# Revit family: QF_ELECTROLUXPROFESSIONAL_587184_PBOT30SDJO
name_source: partatom
category: Attrezzature speciali
units: mm (PartAtom-declared; Revit-internal decimal feet)

## family parameters
Basato su piano di lavoro = No
Condiviso = No
Punto di calcolo locali = No
Quota connettore circolare = Usa diametro
Sempre verticale = Sì
Taglio con vuoti quando caricato = No
Tipo di parte = Normale

## types (1)
- Standard
    Accessory = Sì
    Cold Water Size = 13 mm
    Compressed Air Pressure = 0.0 Pa
    Compressed Air Size = 0 mm
    Compressed Air Volume = 0.0 L/s
    Condensate Return Size = 25 mm
    Cycle = 50 Hz
    Depth Actual = 1000 mm  [stored 3.28084 ft]
    Descrizione = STEAM (ELEC) BOILING PAN,TILTING,300L,230V,FS,MARINE
    Direct Waste Size = 0 mm
    Gas Input Pressure = 0
    Gas KW = 0
    Gas Size = 0 mm
    HP = 0.3 HP
    Height Actual = 700 mm
    Hot Water Size = 13 mm
    Item Number = 587184
    Length Actual = 1500 mm  [stored 4.92126 ft]
    Modello = PBOT30SDJO
    Phase = 1
    Produttore = Electrolux Professional
    Prospetto di default = 0 mm  [stored 0 ft]
    Refrigerant Compressor Remote = Sì
    Refrigeration Liquid Line Size = 0 mm  [stored 0 ft]
    Refrigeration Suction Line Size = 0 mm  [stored 0 ft]
    Steam Consumption per Hour = 105
    Steam Supply Maximum Pressure = 4.9 Pa
    Steam Supply Minimum Pressure = 3.3 Pa
    Steam Supply Size = 25 mm
    URL = https://www.electroluxprofessional.com
    URL Manufacturer = https://www.electroluxprofessional.com
    Volts = 230 V
    Watts = 200 W
    Weight = 390.00 kg

note: source unit labels omitted for Gas Input Pressure — the stored unit's dimension contradicts the parameter name (converter mislabeling)

note: [stored X ft] marks values corroborated as IEEE doubles in the binary element streams (Revit-internal decimal feet)

## geometry (parser evidence)
native form markers: Blend x10, Sweep x10
no freeform markers — native parametric forms only
